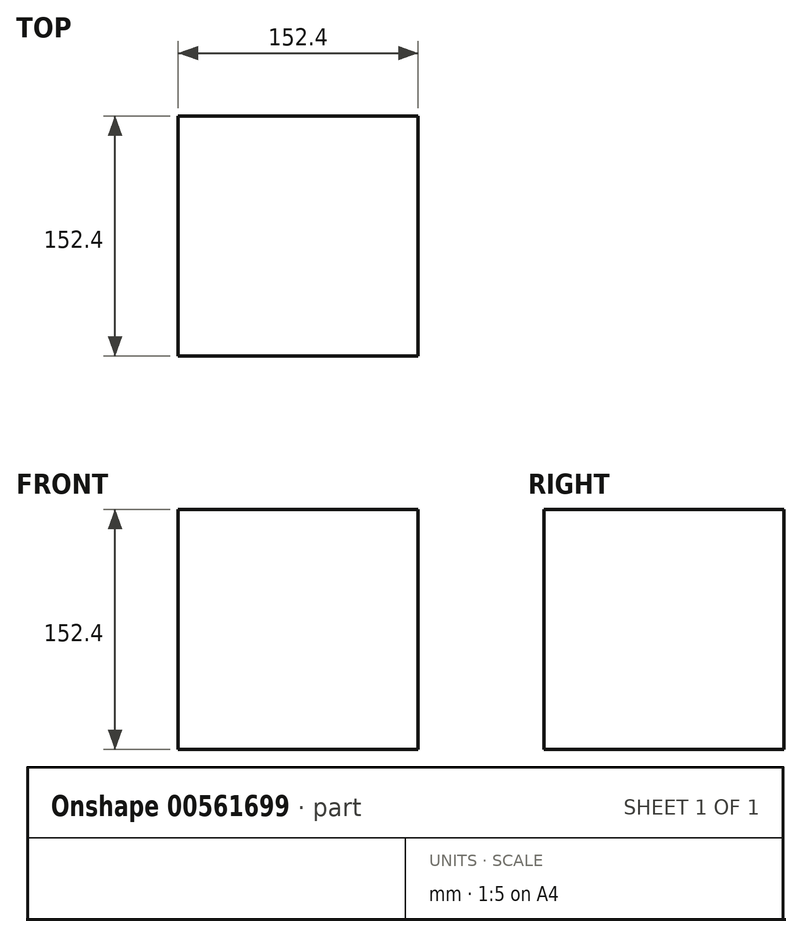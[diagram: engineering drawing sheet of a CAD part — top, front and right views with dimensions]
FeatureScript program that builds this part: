
annotation { "Feature Type Name" : "Feature", "Feature Type Description" : "" }
export const myFeature = defineFeature(function(context is Context, id is Id, definition is map)
    precondition{}
    {
        {
            var Q0;
            Q0=qCreatedBy(makeId("Front.planeOp"),FACE);
            var sketch = newSketch(context, id + "F0", { "sketchPlane" : qUnion([Q0])});
            skLineSegment(sketch, "E0.bottom", {"start": v(-76.2, 76.2) * mm, "end": v(76.2, 76.2) * mm});
            skLineSegment(sketch, "E0.top", {"start": v(-76.2, -76.2) * mm, "end": v(76.2, -76.2) * mm});
            skLineSegment(sketch, "E0.left", {"start": v(-76.2, 76.2) * mm, "end": v(-76.2, -76.2) * mm});
            skLineSegment(sketch, "E0.right", {"start": v(76.2, 76.2) * mm, "end": v(76.2, -76.2) * mm});
            skPoint(sketch, "E0.middle", {"position": v(0, 0) * mm});
            skSolve(sketch);
        }
        {
            var Q0;
            Q0=makeQuery(id+"F0.imprint","IMPRINT",FACE,{"disambiguationData":[TD([[makeQuery(id+"F0.imprint","IMPRINT",EDGE,{"derivedFrom":sQuery(id+"F0.wireOp",EDGE,"E0.bottom")}),-1.0]])]});
            extrude(context, id + "F1", {"entities" : qUnion([Q0]), "oppositeDirection" : true, "depth" : 152.4 * mm, "offsetDistance" : 25.4 * mm});
        }
    });
